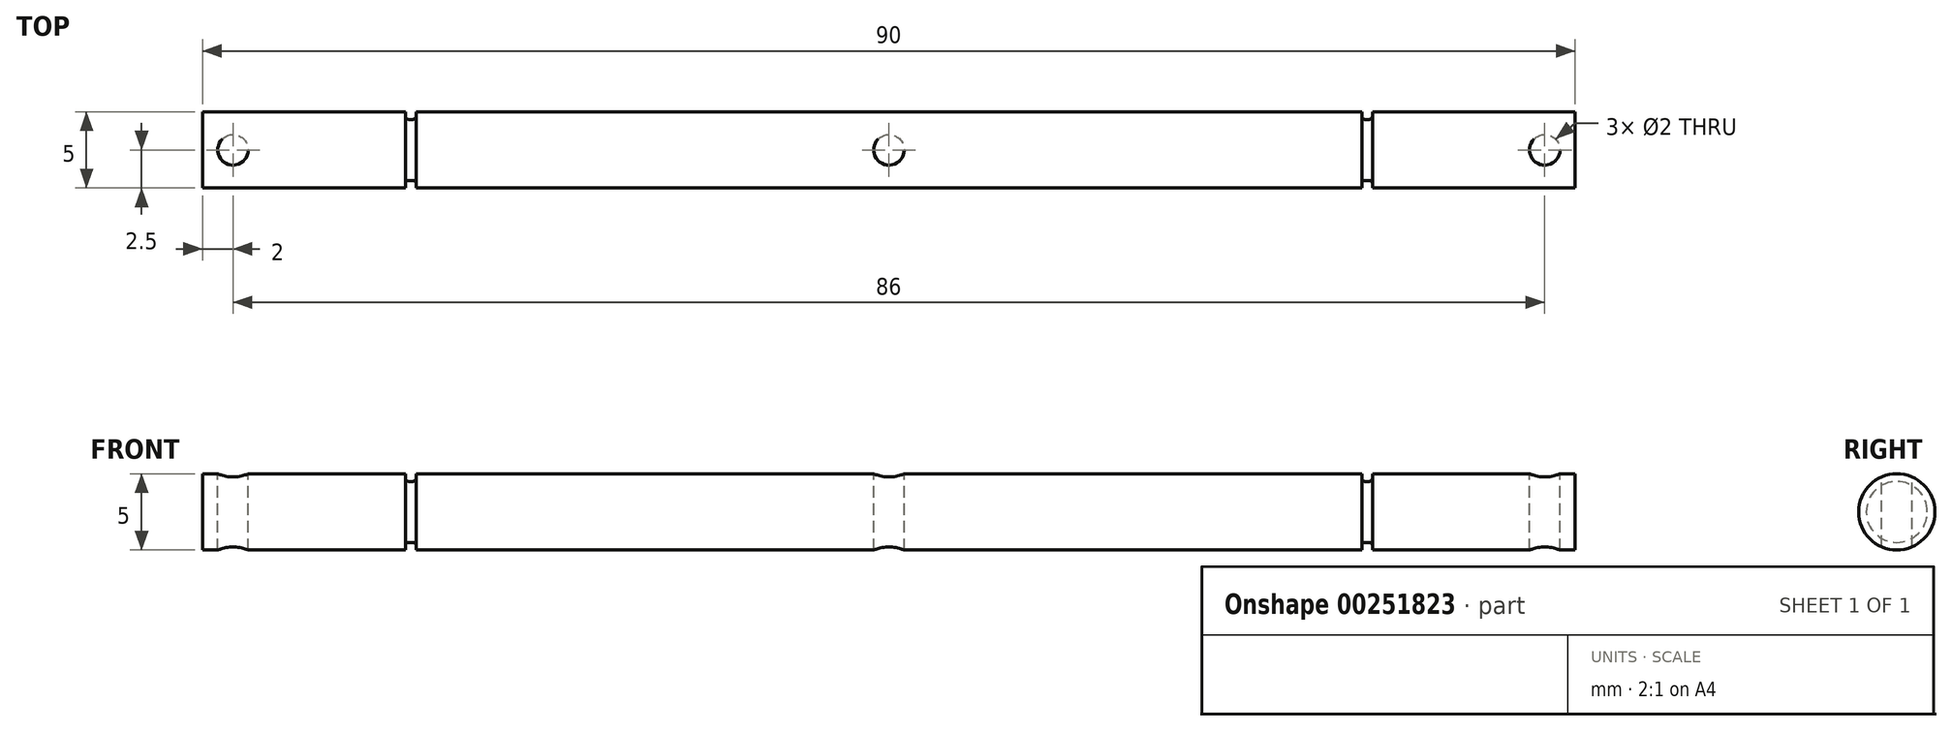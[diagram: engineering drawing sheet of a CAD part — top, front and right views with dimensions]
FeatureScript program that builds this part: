
annotation { "Feature Type Name" : "Feature", "Feature Type Description" : "" }
export const myFeature = defineFeature(function(context is Context, id is Id, definition is map)
    precondition{}
    {
        {
            var Q0;
            Q0=qCreatedBy(makeId("Front.planeOp"),FACE);
            var sketch = newSketch(context, id + "F0", { "sketchPlane" : qUnion([Q0])});
            skLineSegment(sketch, "E0.bottom", {"start": v(-45, 2.5) * mm, "end": v(-31.7, 2.5) * mm});
            skLineSegment(sketch, "E0.top", {"start": v(-45, 0) * mm, "end": v(45, 0) * mm});
            skLineSegment(sketch, "E0.left", {"start": v(-45, 2.5) * mm, "end": v(-45, 0) * mm});
            skLineSegment(sketch, "E0.right", {"start": v(45, 2.5) * mm, "end": v(45, 0) * mm});
            skLineSegment(sketch, "E1", {"start": v(-31.7, 2.5) * mm, "end": v(-31.7, 2.2) * mm});
            skLineSegment(sketch, "E2", {"start": v(-31, 2.5) * mm, "end": v(-31, 2.2) * mm});
            skLineSegment(sketch, "E3", {"start": v(-31.5, 2) * mm, "end": v(-31.2, 2) * mm});
            skPoint(sketch, "E4.visualSharp", {"position": v(-31.7, 2) * mm});
            skArc(sketch, "E4.filletArc", {"start": v(-31.7, 2.2) * mm, "mid": v(-31.64, 2.06) * mm, "end": v(-31.5, 2) * mm});
            skPoint(sketch, "E5.visualSharp", {"position": v(-31, 2) * mm});
            skArc(sketch, "E5.filletArc", {"start": v(-31.2, 2) * mm, "mid": v(-31.06, 2.06) * mm, "end": v(-31, 2.2) * mm});
            skLineSegment(sketch, "E6.MirrorCS", {"start": v(31, 2.5) * mm, "end": v(31, 2.2) * mm});
            skArc(sketch, "E7.MirrorCS", {"start": v(31.2, 2) * mm, "mid": v(31.06, 2.06) * mm, "end": v(31, 2.2) * mm});
            skLineSegment(sketch, "E8.MirrorCS", {"start": v(31.5, 2) * mm, "end": v(31.2, 2) * mm});
            skPoint(sketch, "E9.MirrorP", {"position": v(31.7, 2) * mm});
            skArc(sketch, "E10.MirrorCS", {"start": v(31.7, 2.2) * mm, "mid": v(31.64, 2.06) * mm, "end": v(31.5, 2) * mm});
            skLineSegment(sketch, "E11.MirrorCS", {"start": v(31.7, 2.5) * mm, "end": v(31.7, 2.2) * mm});
            skLineSegment(sketch, "E12.trimOffspring", {"start": v(-31, 2.5) * mm, "end": v(31, 2.5) * mm});
            skLineSegment(sketch, "E13.trimOffspring", {"start": v(31.7, 2.5) * mm, "end": v(45, 2.5) * mm});
            skSolve(sketch);
        }
        {
            var Q0;
            Q0=makeQuery(id+"F0.imprint","IMPRINT",FACE,{"disambiguationData":[TD([[makeQuery(id+"F0.imprint","IMPRINT",EDGE,{"derivedFrom":sQuery(id+"F0.wireOp",EDGE,"E0.bottom")}),-1.0]])]});
            var Q1;
            Q1=sQuery(id+"F0.wireOp",EDGE,"E0.top");
            revolve(context, id + "F1", {"entities" : qUnion([Q0]), "axis" : qUnion([Q1]), "revolveType" : RevolveType.FULL});
        }
        {
            var Q0;
            Q0=qCreatedBy(makeId("Top.planeOp"),FACE);
            var sketch = newSketch(context, id + "F2", { "sketchPlane" : qUnion([Q0])});
            skCircle(sketch, "E14", {"center": v(-43, 0) * mm, "radius": 1 * mm});
            skCircle(sketch, "E15", {"center": v(0, 0) * mm, "radius": 1 * mm});
            skCircle(sketch, "E16", {"center": v(43, 0) * mm, "radius": 1 * mm});
            skSolve(sketch);
        }
        {
            var Q0;
            Q0 = qSketchRegion(id + "F2", true);
            extrude(context, id + "F3", {"entities" : qUnion([Q0]), "operationType" : NewBodyOperationType.REMOVE, "endBound" : BoundingType.SYMMETRIC, "oppositeDirection" : true, "depth" : 25 * mm});
        }
    });
